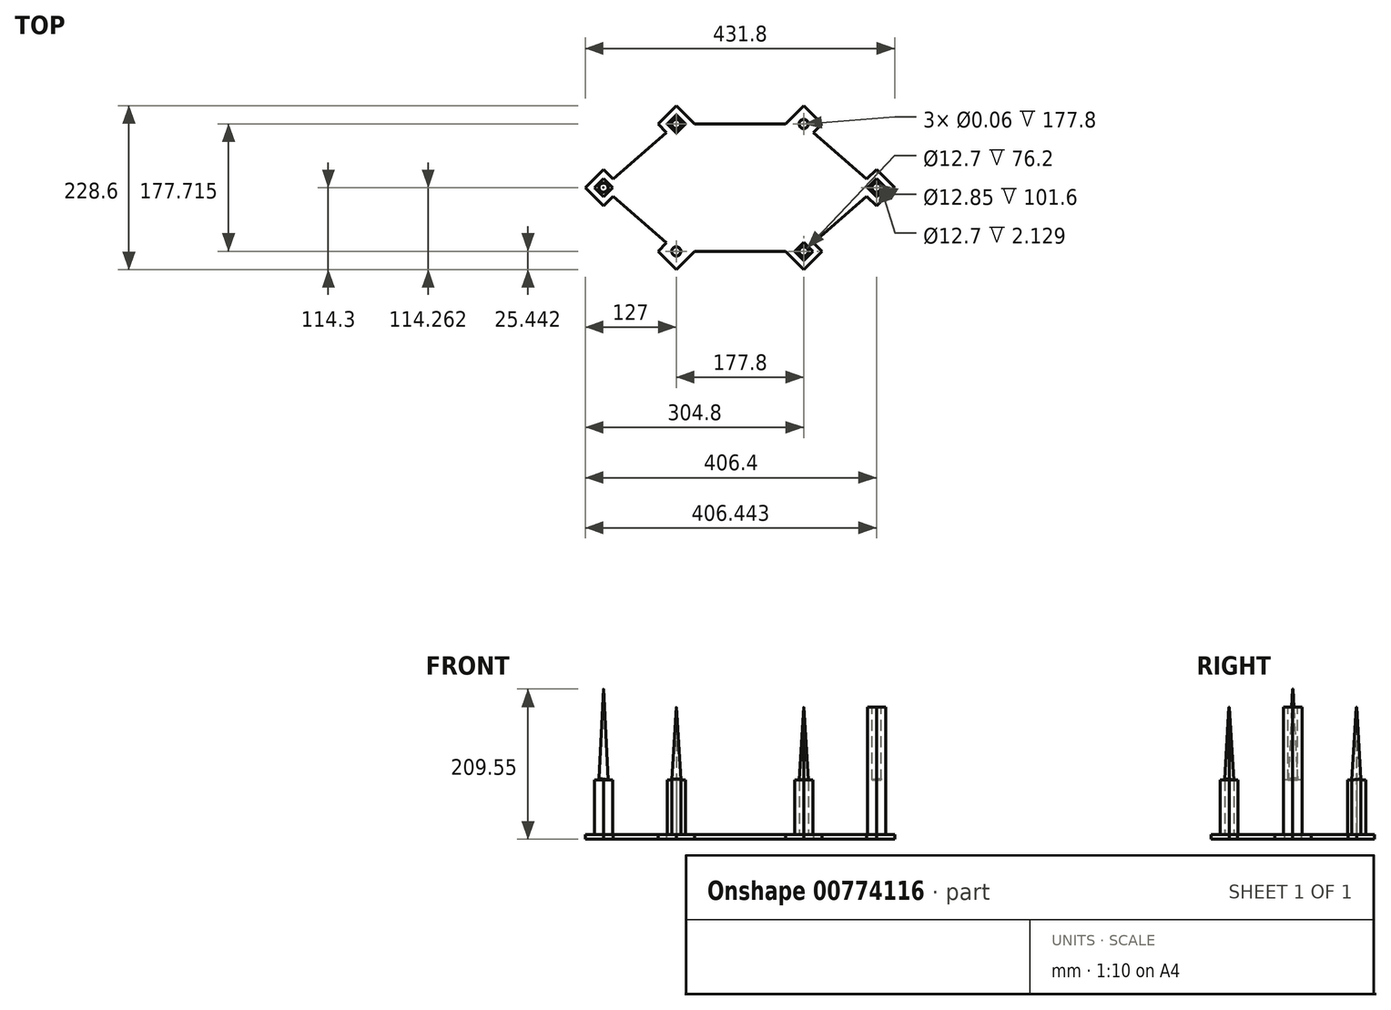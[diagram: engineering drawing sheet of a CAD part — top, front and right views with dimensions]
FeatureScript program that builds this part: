
annotation { "Feature Type Name" : "Feature", "Feature Type Description" : "" }
export const myFeature = defineFeature(function(context is Context, id is Id, definition is map)
    precondition{}
    {
        {
            var Q0;
            Q0=qCreatedBy(makeId("Top.planeOp"),FACE);
            var sketch = newSketch(context, id + "F0", { "sketchPlane" : qUnion([Q0])});
            skLineSegment(sketch, "E0", {"start": v(0, 88.9) * mm, "end": v(-63.5, 88.9) * mm});
            skLineSegment(sketch, "E1", {"start": v(-63.5, 88.9) * mm, "end": v(-88.9, 114.3) * mm});
            skLineSegment(sketch, "E2", {"start": v(-88.9, 114.3) * mm, "end": v(-114.3, 88.9) * mm});
            skLineSegment(sketch, "E3", {"start": v(-114.3, 88.9) * mm, "end": v(-88.9, 63.5) * mm});
            skLineSegment(sketch, "E4", {"start": v(-88.9, 63.5) * mm, "end": v(-63.5, 88.9) * mm});
            skLineSegment(sketch, "E5", {"start": v(-88.9, 63.5) * mm, "end": v(-88.9, 0) * mm});
            skLineSegment(sketch, "E6", {"start": v(-88.9, 88.9) * mm, "end": v(-190.5, 0) * mm});
            skLineSegment(sketch, "E7", {"start": v(-88.9, 114.3) * mm, "end": v(-88.9, 63.5) * mm, "construction": true});
            skLineSegment(sketch, "E8", {"start": v(-63.5, 88.9) * mm, "end": v(-114.3, 88.9) * mm, "construction": true});
            skLineSegment(sketch, "E9", {"start": v(-190.5, 25.4) * mm, "end": v(-215.9, 0) * mm});
            skLineSegment(sketch, "E10", {"start": v(-190.5, 25.4) * mm, "end": v(-165.1, 0) * mm});
            skLineSegment(sketch, "E11", {"start": v(-190.5, 25.4) * mm, "end": v(-190.5, 0) * mm, "construction": true});
            skPoint(sketch, "E12", {"position": v(-190.5, 0) * mm});
            skLineSegment(sketch, "E13.MirrorCS", {"start": v(-114.3, -88.9) * mm, "end": v(-88.9, -63.5) * mm});
            skLineSegment(sketch, "E14.MirrorCS", {"start": v(-88.9, -63.5) * mm, "end": v(-63.5, -88.9) * mm});
            skLineSegment(sketch, "E15.MirrorCS", {"start": v(-63.5, -88.9) * mm, "end": v(-114.3, -88.9) * mm, "construction": true});
            skLineSegment(sketch, "E16.MirrorCS", {"start": v(-190.5, -25.4) * mm, "end": v(-165.1, 0) * mm});
            skLineSegment(sketch, "E17.MirrorCS", {"start": v(-63.5, -88.9) * mm, "end": v(-88.9, -114.3) * mm});
            skLineSegment(sketch, "E18.MirrorCS", {"start": v(-88.9, -114.3) * mm, "end": v(-88.9, -63.5) * mm, "construction": true});
            skLineSegment(sketch, "E19.MirrorCS", {"start": v(0, -88.9) * mm, "end": v(-63.5, -88.9) * mm});
            skLineSegment(sketch, "E20.MirrorCS", {"start": v(-88.9, -114.3) * mm, "end": v(-114.3, -88.9) * mm});
            skLineSegment(sketch, "E21.MirrorCS", {"start": v(-190.5, -25.4) * mm, "end": v(-215.9, 0) * mm});
            skLineSegment(sketch, "E22.MirrorCS", {"start": v(-88.9, -88.9) * mm, "end": v(-190.5, 0) * mm});
            skLineSegment(sketch, "E23.MirrorCS", {"start": v(-190.5, -25.4) * mm, "end": v(-190.5, 0) * mm, "construction": true});
            skLineSegment(sketch, "E24.MirrorCS", {"start": v(-88.9, -63.5) * mm, "end": v(-88.9, 0) * mm});
            skPoint(sketch, "E25.MirrorP", {"position": v(190.5, 0) * mm});
            skLineSegment(sketch, "E26.MirrorCS", {"start": v(63.5, 88.9) * mm, "end": v(114.3, 88.9) * mm, "construction": true});
            skLineSegment(sketch, "E27.MirrorCS", {"start": v(190.5, 25.4) * mm, "end": v(215.9, 0) * mm});
            skLineSegment(sketch, "E28.MirrorCS", {"start": v(63.5, -88.9) * mm, "end": v(114.3, -88.9) * mm, "construction": true});
            skLineSegment(sketch, "E29.MirrorCS", {"start": v(88.9, -63.5) * mm, "end": v(63.5, -88.9) * mm});
            skLineSegment(sketch, "E30.MirrorCS", {"start": v(190.5, 25.4) * mm, "end": v(165.1, 0) * mm});
            skLineSegment(sketch, "E31.MirrorCS", {"start": v(190.5, 25.4) * mm, "end": v(190.5, 0) * mm, "construction": true});
            skLineSegment(sketch, "E32.MirrorCS", {"start": v(114.3, -88.9) * mm, "end": v(88.9, -63.5) * mm});
            skLineSegment(sketch, "E33.MirrorCS", {"start": v(88.9, -63.5) * mm, "end": v(88.9, 0) * mm});
            skLineSegment(sketch, "E34.MirrorCS", {"start": v(190.5, -25.4) * mm, "end": v(190.5, 0) * mm, "construction": true});
            skLineSegment(sketch, "E35.MirrorCS", {"start": v(190.5, -25.4) * mm, "end": v(215.9, 0) * mm});
            skLineSegment(sketch, "E36.MirrorCS", {"start": v(190.5, -25.4) * mm, "end": v(165.1, 0) * mm});
            skLineSegment(sketch, "E37.MirrorCS", {"start": v(0, 88.9) * mm, "end": v(63.5, 88.9) * mm});
            skLineSegment(sketch, "E38.MirrorCS", {"start": v(114.3, 88.9) * mm, "end": v(88.9, 63.5) * mm});
            skLineSegment(sketch, "E39.MirrorCS", {"start": v(88.9, 63.5) * mm, "end": v(63.5, 88.9) * mm});
            skLineSegment(sketch, "E40.MirrorCS", {"start": v(88.9, -88.9) * mm, "end": v(190.5, 0) * mm});
            skLineSegment(sketch, "E41.MirrorCS", {"start": v(88.9, 114.3) * mm, "end": v(88.9, 63.5) * mm, "construction": true});
            skLineSegment(sketch, "E42.MirrorCS", {"start": v(0, -88.9) * mm, "end": v(63.5, -88.9) * mm});
            skLineSegment(sketch, "E43.MirrorCS", {"start": v(63.5, 88.9) * mm, "end": v(88.9, 114.3) * mm});
            skLineSegment(sketch, "E44.MirrorCS", {"start": v(88.9, 114.3) * mm, "end": v(114.3, 88.9) * mm});
            skLineSegment(sketch, "E45.MirrorCS", {"start": v(63.5, -88.9) * mm, "end": v(88.9, -114.3) * mm});
            skLineSegment(sketch, "E46.MirrorCS", {"start": v(88.9, 88.9) * mm, "end": v(190.5, 0) * mm});
            skLineSegment(sketch, "E47.MirrorCS", {"start": v(88.9, -114.3) * mm, "end": v(114.3, -88.9) * mm});
            skLineSegment(sketch, "E48.MirrorCS", {"start": v(88.9, 63.5) * mm, "end": v(88.9, 0) * mm});
            skLineSegment(sketch, "E49.MirrorCS", {"start": v(88.9, -114.3) * mm, "end": v(88.9, -63.5) * mm, "construction": true});
            skSolve(sketch);
        }
        {
            var Q0;
            {var subQ5=sQuery(id+"F0.wireOp",EDGE,"E9");Q0=makeQuery(id+"F0.imprint","IMPRINT",FACE,{"disambiguationData":[TD([[makeQuery(id+"F0.imprint","IMPRINT",EDGE,{"derivedFrom":subQ5}),1.0]])]});}
            var Q1;
            {var subQ0=sQuery(id+"F0.wireOp",EDGE,"E22.MirrorCS");var subQ1=sQuery(id+"F0.wireOp",EDGE,"E6");var subQ2=makeQuery(id+"F0.imprint","INTERSECT",VERTEX,{"derivedFrom":[subQ1,subQ0]});Q1=makeQuery(id+"F0.imprint","IMPRINT",FACE,{"disambiguationData":[TD([[makeQuery(id+"F0.imprint","IMPRINT",EDGE,{"disambiguationData":[TD([[subQ2,1.0]])],"derivedFrom":subQ1}),1.0]])]});}
            var Q2;
            {var subQ7=sQuery(id+"F0.wireOp",EDGE,"E5");Q2=makeQuery(id+"F0.imprint","IMPRINT",FACE,{"disambiguationData":[TD([[makeQuery(id+"F0.imprint","IMPRINT",EDGE,{"derivedFrom":subQ7}),-1.0]])]});}
            var Q3;
            Q3=makeQuery(id+"F0.imprint","IMPRINT",FACE,{"disambiguationData":[TD([[makeQuery(id+"F0.imprint","IMPRINT",EDGE,{"derivedFrom":sQuery(id+"F0.wireOp",EDGE,"E1")}),1.0]])]});
            var Q4;
            {var subQ0=sQuery(id+"F0.wireOp",EDGE,"E14.MirrorCS");Q4=makeQuery(id+"F0.imprint","IMPRINT",FACE,{"disambiguationData":[TD([[makeQuery(id+"F0.imprint","IMPRINT",EDGE,{"derivedFrom":subQ0}),-1.0]])]});}
            var Q5;
            {var subQ1=sQuery(id+"F0.wireOp",EDGE,"E29.MirrorCS");Q5=makeQuery(id+"F0.imprint","IMPRINT",FACE,{"disambiguationData":[TD([[makeQuery(id+"F0.imprint","IMPRINT",EDGE,{"derivedFrom":subQ1}),1.0]])]});}
            var Q6;
            {var subQ9=sQuery(id+"F0.wireOp",EDGE,"E33.MirrorCS");Q6=makeQuery(id+"F0.imprint","IMPRINT",FACE,{"disambiguationData":[TD([[makeQuery(id+"F0.imprint","IMPRINT",EDGE,{"derivedFrom":subQ9}),-1.0]])]});}
            var Q7;
            Q7=makeQuery(id+"F0.imprint","IMPRINT",FACE,{"disambiguationData":[TD([[makeQuery(id+"F0.imprint","IMPRINT",EDGE,{"derivedFrom":sQuery(id+"F0.wireOp",EDGE,"E0")}),1.0]])]});
            var Q8;
            {var subQ0=sQuery(id+"F0.wireOp",EDGE,"E39.MirrorCS");Q8=makeQuery(id+"F0.imprint","IMPRINT",FACE,{"disambiguationData":[TD([[makeQuery(id+"F0.imprint","IMPRINT",EDGE,{"derivedFrom":subQ0}),-1.0]])]});}
            var Q9;
            {var subQ5=sQuery(id+"F0.wireOp",EDGE,"E27.MirrorCS");Q9=makeQuery(id+"F0.imprint","IMPRINT",FACE,{"disambiguationData":[TD([[makeQuery(id+"F0.imprint","IMPRINT",EDGE,{"derivedFrom":subQ5}),-1.0]])]});}
            var Q10;
            {var subQ0=sQuery(id+"F0.wireOp",EDGE,"E36.MirrorCS");var subQ1=sQuery(id+"F0.wireOp",EDGE,"E30.MirrorCS");var subQ2=makeQuery(id+"F0.imprint","INTERSECT",VERTEX,{"derivedFrom":[subQ1,subQ0]});Q10=makeQuery(id+"F0.imprint","IMPRINT",FACE,{"disambiguationData":[TD([[makeQuery(id+"F0.imprint","IMPRINT",EDGE,{"disambiguationData":[TD([[subQ2,1.0]])],"derivedFrom":subQ1}),1.0]])]});}
            extrude(context, id + "F1", {"entities" : qUnion([Q0, Q1, Q2, Q3, Q4, Q5, Q6, Q7, Q8, Q9, Q10]), "depth" : 228.6 * mm, "offsetDistance" : 25.4 * mm});
        }
        {
            var Q0;
            Q0=makeQuery(id+"F1.opExtrude","CAP_FACE",FACE,{"disambiguationData":[OSD([sQuery(id+"F0.wireOp",EDGE,"E0"),sQuery(id+"F0.wireOp",EDGE,"E1"),sQuery(id+"F0.wireOp",EDGE,"E2"),sQuery(id+"F0.wireOp",EDGE,"E3"),sQuery(id+"F0.wireOp",EDGE,"E6"),sQuery(id+"F0.wireOp",EDGE,"E9"),sQuery(id+"F0.wireOp",EDGE,"E10"),sQuery(id+"F0.wireOp",EDGE,"E13.MirrorCS"),sQuery(id+"F0.wireOp",EDGE,"E16.MirrorCS"),sQuery(id+"F0.wireOp",EDGE,"E17.MirrorCS"),sQuery(id+"F0.wireOp",EDGE,"E19.MirrorCS"),sQuery(id+"F0.wireOp",EDGE,"E20.MirrorCS"),sQuery(id+"F0.wireOp",EDGE,"E21.MirrorCS"),sQuery(id+"F0.wireOp",EDGE,"E22.MirrorCS"),sQuery(id+"F0.wireOp",EDGE,"E27.MirrorCS"),sQuery(id+"F0.wireOp",EDGE,"E30.MirrorCS"),sQuery(id+"F0.wireOp",EDGE,"E32.MirrorCS"),sQuery(id+"F0.wireOp",EDGE,"E35.MirrorCS"),sQuery(id+"F0.wireOp",EDGE,"E36.MirrorCS"),sQuery(id+"F0.wireOp",EDGE,"E37.MirrorCS"),sQuery(id+"F0.wireOp",EDGE,"E38.MirrorCS"),sQuery(id+"F0.wireOp",EDGE,"E40.MirrorCS"),sQuery(id+"F0.wireOp",EDGE,"E42.MirrorCS"),sQuery(id+"F0.wireOp",EDGE,"E43.MirrorCS"),sQuery(id+"F0.wireOp",EDGE,"E44.MirrorCS"),sQuery(id+"F0.wireOp",EDGE,"E45.MirrorCS"),sQuery(id+"F0.wireOp",EDGE,"E46.MirrorCS"),sQuery(id+"F0.wireOp",EDGE,"E47.MirrorCS")])],"isStart":false});
            var sketch = newSketch(context, id + "F2", { "sketchPlane" : qUnion([Q0])});
            skLineSegment(sketch, "E50", {"start": v(-101.6, 88.9) * mm, "end": v(-88.9, 76.2) * mm});
            skLineSegment(sketch, "E51", {"start": v(-88.9, 76.2) * mm, "end": v(-76.2, 88.9) * mm});
            skLineSegment(sketch, "E52", {"start": v(-76.2, 88.9) * mm, "end": v(-88.9, 101.6) * mm});
            skLineSegment(sketch, "E53", {"start": v(-88.9, 101.6) * mm, "end": v(-101.6, 88.9) * mm});
            skCircle(sketch, "E54", {"center": v(-88.9, 88.86) * mm, "radius": 6.35 * mm});
            skCircle(sketch, "E55", {"center": v(-88.9, 88.86) * mm, "radius": 0.03 * mm});
            skCircle(sketch, "E56.MirrorC", {"center": v(-88.9, -88.86) * mm, "radius": 0.03 * mm});
            skCircle(sketch, "E57.MirrorC", {"center": v(-88.9, -88.86) * mm, "radius": 6.35 * mm});
            skLineSegment(sketch, "E58.MirrorCS", {"start": v(-88.9, -101.6) * mm, "end": v(-101.6, -88.9) * mm});
            skLineSegment(sketch, "E59.MirrorCS", {"start": v(-76.2, -88.9) * mm, "end": v(-88.9, -101.6) * mm});
            skLineSegment(sketch, "E60.MirrorCS", {"start": v(-88.9, -76.2) * mm, "end": v(-76.2, -88.9) * mm});
            skLineSegment(sketch, "E61.MirrorCS", {"start": v(-101.6, -88.9) * mm, "end": v(-88.9, -76.2) * mm});
            skCircle(sketch, "E62.MirrorC", {"center": v(88.9, 88.86) * mm, "radius": 0.03 * mm});
            skCircle(sketch, "E63.MirrorC", {"center": v(88.9, -88.86) * mm, "radius": 0.03 * mm});
            skCircle(sketch, "E64.MirrorC", {"center": v(88.9, 88.86) * mm, "radius": 6.35 * mm});
            skLineSegment(sketch, "E65.MirrorCS", {"start": v(88.9, 101.6) * mm, "end": v(101.6, 88.9) * mm});
            skLineSegment(sketch, "E66.MirrorCS", {"start": v(76.2, 88.9) * mm, "end": v(88.9, 101.6) * mm});
            skLineSegment(sketch, "E67.MirrorCS", {"start": v(88.9, 76.2) * mm, "end": v(76.2, 88.9) * mm});
            skLineSegment(sketch, "E68.MirrorCS", {"start": v(101.6, 88.9) * mm, "end": v(88.9, 76.2) * mm});
            skLineSegment(sketch, "E69.MirrorCS", {"start": v(101.6, -88.9) * mm, "end": v(88.9, -76.2) * mm});
            skLineSegment(sketch, "E70.MirrorCS", {"start": v(76.2, -88.9) * mm, "end": v(88.9, -101.6) * mm});
            skLineSegment(sketch, "E71.MirrorCS", {"start": v(88.9, -76.2) * mm, "end": v(76.2, -88.9) * mm});
            skCircle(sketch, "E72.MirrorC", {"center": v(88.9, -88.86) * mm, "radius": 6.35 * mm});
            skLineSegment(sketch, "E73.MirrorCS", {"start": v(88.9, -101.6) * mm, "end": v(101.6, -88.9) * mm});
            skLineSegment(sketch, "E74", {"start": v(-190.5, 12.7) * mm, "end": v(-203.2, 0) * mm});
            skLineSegment(sketch, "E75", {"start": v(-203.2, 0) * mm, "end": v(-190.5, -12.7) * mm});
            skLineSegment(sketch, "E76", {"start": v(-190.5, -12.7) * mm, "end": v(-177.8, 0) * mm});
            skLineSegment(sketch, "E77", {"start": v(-190.5, 12.7) * mm, "end": v(-177.8, 0) * mm});
            skCircle(sketch, "E78", {"center": v(-190.5, 0) * mm, "radius": 6.35 * mm});
            skCircle(sketch, "E79.MirrorC", {"center": v(190.5, 0) * mm, "radius": 6.35 * mm});
            skLineSegment(sketch, "E80.MirrorCS", {"start": v(203.2, 0) * mm, "end": v(190.5, -12.7) * mm});
            skLineSegment(sketch, "E81.MirrorCS", {"start": v(190.5, 12.7) * mm, "end": v(177.8, 0) * mm});
            skLineSegment(sketch, "E82.MirrorCS", {"start": v(190.5, -12.7) * mm, "end": v(177.8, 0) * mm});
            skLineSegment(sketch, "E83.MirrorCS", {"start": v(190.5, 12.7) * mm, "end": v(203.2, 0) * mm});
            skSolve(sketch);
        }
        {
            var Q0;
            Q0=makeQuery(id+"F2.imprint","IMPRINT",FACE,{"disambiguationData":[TD([[makeQuery(id+"F2.imprint","IMPRINT",EDGE,{"derivedFrom":sQuery(id+"F2.wireOp",EDGE,"E74")}),1.0]])]});
            var Q1;
            Q1=makeQuery(id+"F2.imprint","IMPRINT",FACE,{"disambiguationData":[TD([[makeQuery(id+"F2.imprint","IMPRINT",EDGE,{"derivedFrom":sQuery(id+"F2.wireOp",EDGE,"E50")}),1.0]])]});
            var Q2;
            Q2=makeQuery(id+"F2.imprint","IMPRINT",FACE,{"disambiguationData":[TD([[makeQuery(id+"F2.imprint","IMPRINT",EDGE,{"derivedFrom":sQuery(id+"F2.wireOp",EDGE,"E79.MirrorC")}),1.0]])]});
            var Q3;
            Q3=makeQuery(id+"F2.imprint","IMPRINT",FACE,{"disambiguationData":[TD([[makeQuery(id+"F2.imprint","IMPRINT",EDGE,{"derivedFrom":sQuery(id+"F2.wireOp",EDGE,"E69.MirrorCS")}),1.0]])]});
            var Q4;
            Q4=makeQuery(id+"F2.imprint","IMPRINT",FACE,{"disambiguationData":[TD([[makeQuery(id+"F2.imprint","IMPRINT",EDGE,{"derivedFrom":sQuery(id+"F2.wireOp",EDGE,"E57.MirrorC")}),1.0]])]});
            var Q5;
            Q5=makeQuery(id+"F2.imprint","IMPRINT",FACE,{"disambiguationData":[TD([[makeQuery(id+"F2.imprint","IMPRINT",EDGE,{"derivedFrom":sQuery(id+"F2.wireOp",EDGE,"E64.MirrorC")}),1.0]])]});
            extrude(context, id + "F3", {"entities" : qUnion([Q0, Q1, Q2, Q3, Q4, Q5]), "operationType" : NewBodyOperationType.ADD, "depth" : 76.2 * mm, "offsetDistance" : 25.4 * mm});
        }
        {
            var Q0;
            Q0=makeQuery(id+"F2.imprint","IMPRINT",FACE,{"disambiguationData":[TD([[makeQuery(id+"F2.imprint","IMPRINT",EDGE,{"derivedFrom":sQuery(id+"F2.wireOp",EDGE,"E54")}),1.0]])]});
            var Q1;
            Q1=makeQuery(id+"F2.imprint","IMPRINT",FACE,{"disambiguationData":[TD([[makeQuery(id+"F2.imprint","IMPRINT",EDGE,{"derivedFrom":sQuery(id+"F2.wireOp",EDGE,"E79.MirrorC")}),-1.0]])]});
            var Q2;
            Q2=makeQuery(id+"F2.imprint","IMPRINT",FACE,{"disambiguationData":[TD([[makeQuery(id+"F2.imprint","IMPRINT",EDGE,{"derivedFrom":sQuery(id+"F2.wireOp",EDGE,"E56.MirrorC")}),-1.0]])]});
            var Q3;
            Q3=makeQuery(id+"F2.imprint","IMPRINT",FACE,{"disambiguationData":[TD([[makeQuery(id+"F2.imprint","IMPRINT",EDGE,{"derivedFrom":sQuery(id+"F2.wireOp",EDGE,"E63.MirrorC")}),1.0]])]});
            var Q4;
            Q4=makeQuery(id+"F2.imprint","IMPRINT",FACE,{"disambiguationData":[TD([[makeQuery(id+"F2.imprint","IMPRINT",EDGE,{"derivedFrom":sQuery(id+"F2.wireOp",EDGE,"E62.MirrorC")}),-1.0]])]});
            extrude(context, id + "F4", {"entities" : qUnion([Q0, Q1, Q2, Q3, Q4]), "operationType" : NewBodyOperationType.ADD, "depth" : 177.8 * mm, "offsetDistance" : 25.4 * mm});
        }
        {
            var Q0;
            Q0=makeQuery(id+"F2.imprint","IMPRINT",FACE,{"disambiguationData":[TD([[makeQuery(id+"F2.imprint","IMPRINT",EDGE,{"derivedFrom":sQuery(id+"F2.wireOp",EDGE,"E78")}),1.0]])]});
            extrude(context, id + "F5", {"entities" : qUnion([Q0]), "operationType" : NewBodyOperationType.ADD, "depth" : 203.2 * mm, "offsetDistance" : 25.4 * mm});
        }
        {
            var Q0;
            Q0=makeQuery(id+"F1.opExtrude","SWEPT_FACE",FACE,{"disambiguationData":[OSD([sQuery(id+"F0.wireOp",EDGE,"E19.MirrorCS"),sQuery(id+"F0.wireOp",EDGE,"E42.MirrorCS")])]});
            var sketch = newSketch(context, id + "F6", { "sketchPlane" : qUnion([Q0])});
            skLineSegment(sketch, "E84.bottom", {"start": v(-88.9, 304.8) * mm, "end": v(-82.5, 304.8) * mm});
            skLineSegment(sketch, "E84.top", {"start": v(-88.9, 406.4) * mm, "end": v(-82.5, 406.4) * mm});
            skLineSegment(sketch, "E84.left", {"start": v(-88.9, 304.8) * mm, "end": v(-88.9, 406.4) * mm});
            skLineSegment(sketch, "E84.right", {"start": v(-82.5, 304.8) * mm, "end": v(-82.5, 406.4) * mm});
            skLineSegment(sketch, "E85", {"start": v(-88.87, 406.4) * mm, "end": v(-82.5, 304.8) * mm});
            skSolve(sketch);
        }
        {
            var Q0;
            {var subQ0=sQuery(id+"F6.wireOp",EDGE,"E84.right");Q0=makeQuery(id+"F6.imprint","IMPRINT",FACE,{"disambiguationData":[TD([[makeQuery(id+"F6.imprint","IMPRINT",EDGE,{"derivedFrom":subQ0}),1.0]])]});}
            var Q1;
            Q1=sQuery(id+"F6.wireOp",EDGE,"E84.left");
            revolve(context, id + "F7", {"operationType" : NewBodyOperationType.REMOVE, "surfaceOperationType" : NewSurfaceOperationType.NEW, "entities" : qUnion([Q0]), "axis" : qUnion([Q1]), "revolveType" : RevolveType.FULL, "oppositeDirection" : true});
        }
        {
            var Q0;
            Q0=makeQuery(id+"F1.opExtrude","SWEPT_FACE",FACE,{"disambiguationData":[OSD([sQuery(id+"F0.wireOp",EDGE,"E19.MirrorCS"),sQuery(id+"F0.wireOp",EDGE,"E42.MirrorCS")])]});
            var sketch = newSketch(context, id + "F8", { "sketchPlane" : qUnion([Q0])});
            skLineSegment(sketch, "E86.bottom", {"start": v(88.9, 304.8) * mm, "end": v(95.3, 304.8) * mm});
            skLineSegment(sketch, "E86.top", {"start": v(88.9, 406.4) * mm, "end": v(95.3, 406.4) * mm});
            skLineSegment(sketch, "E86.left", {"start": v(88.9, 304.8) * mm, "end": v(88.9, 406.4) * mm});
            skLineSegment(sketch, "E86.right", {"start": v(95.3, 304.8) * mm, "end": v(95.3, 406.4) * mm});
            skLineSegment(sketch, "E87", {"start": v(88.93, 406.4) * mm, "end": v(95.3, 304.8) * mm});
            skSolve(sketch);
        }
        {
            var Q0;
            {var subQ0=sQuery(id+"F8.wireOp",EDGE,"E86.right");Q0=makeQuery(id+"F8.imprint","IMPRINT",FACE,{"disambiguationData":[TD([[makeQuery(id+"F8.imprint","IMPRINT",EDGE,{"derivedFrom":subQ0}),1.0]])]});}
            var Q1;
            Q1=sQuery(id+"F8.wireOp",EDGE,"E86.left");
            revolve(context, id + "F9", {"operationType" : NewBodyOperationType.REMOVE, "surfaceOperationType" : NewSurfaceOperationType.NEW, "entities" : qUnion([Q0]), "axis" : qUnion([Q1]), "revolveType" : RevolveType.FULL, "oppositeDirection" : true});
        }
        {
            var Q0;
            Q0=makeQuery(id+"F1.opExtrude","SWEPT_FACE",FACE,{"disambiguationData":[OSD([sQuery(id+"F0.wireOp",EDGE,"E0"),sQuery(id+"F0.wireOp",EDGE,"E37.MirrorCS")])]});
            var sketch = newSketch(context, id + "F10", { "sketchPlane" : qUnion([Q0])});
            skLineSegment(sketch, "E88.bottom", {"start": v(88.9, 304.8) * mm, "end": v(95.3, 304.8) * mm});
            skLineSegment(sketch, "E88.top", {"start": v(88.9, 406.4) * mm, "end": v(95.3, 406.4) * mm});
            skLineSegment(sketch, "E88.left", {"start": v(88.9, 304.8) * mm, "end": v(88.9, 406.4) * mm});
            skLineSegment(sketch, "E88.right", {"start": v(95.3, 304.8) * mm, "end": v(95.3, 406.4) * mm});
            skLineSegment(sketch, "E89", {"start": v(88.93, 406.4) * mm, "end": v(95.3, 304.8) * mm});
            skSolve(sketch);
        }
        {
            var Q0;
            {var subQ0=sQuery(id+"F10.wireOp",EDGE,"E88.right");Q0=makeQuery(id+"F10.imprint","IMPRINT",FACE,{"disambiguationData":[TD([[makeQuery(id+"F10.imprint","IMPRINT",EDGE,{"derivedFrom":subQ0}),1.0]])]});}
            var Q1;
            Q1=sQuery(id+"F10.wireOp",EDGE,"E88.left");
            revolve(context, id + "F11", {"operationType" : NewBodyOperationType.REMOVE, "surfaceOperationType" : NewSurfaceOperationType.NEW, "entities" : qUnion([Q0]), "axis" : qUnion([Q1]), "revolveType" : RevolveType.FULL, "oppositeDirection" : true});
        }
        {
            var Q0;
            Q0=makeQuery(id+"F1.opExtrude","SWEPT_FACE",FACE,{"disambiguationData":[OSD([sQuery(id+"F0.wireOp",EDGE,"E0"),sQuery(id+"F0.wireOp",EDGE,"E37.MirrorCS")])]});
            var sketch = newSketch(context, id + "F12", { "sketchPlane" : qUnion([Q0])});
            skLineSegment(sketch, "E90.bottom", {"start": v(-82.5, 304.8) * mm, "end": v(-88.9, 304.8) * mm});
            skLineSegment(sketch, "E90.top", {"start": v(-82.5, 406.4) * mm, "end": v(-88.9, 406.4) * mm});
            skLineSegment(sketch, "E90.left", {"start": v(-82.5, 304.8) * mm, "end": v(-82.5, 406.4) * mm});
            skLineSegment(sketch, "E90.right", {"start": v(-88.9, 304.8) * mm, "end": v(-88.9, 406.4) * mm});
            skLineSegment(sketch, "E91", {"start": v(-88.87, 406.4) * mm, "end": v(-82.5, 304.8) * mm});
            skSolve(sketch);
        }
        {
            var Q0;
            {var subQ0=sQuery(id+"F12.wireOp",EDGE,"E90.left");Q0=makeQuery(id+"F12.imprint","IMPRINT",FACE,{"disambiguationData":[TD([[makeQuery(id+"F12.imprint","IMPRINT",EDGE,{"derivedFrom":subQ0}),1.0]])]});}
            var Q1;
            Q1=sQuery(id+"F12.wireOp",EDGE,"E90.right");
            revolve(context, id + "F13", {"operationType" : NewBodyOperationType.REMOVE, "surfaceOperationType" : NewSurfaceOperationType.NEW, "entities" : qUnion([Q0]), "axis" : qUnion([Q1]), "revolveType" : RevolveType.FULL, "oppositeDirection" : true});
        }
        {
            var Q0;
            Q0=makeQuery(id+"F1.opExtrude","SWEPT_FACE",FACE,{"disambiguationData":[OSD([sQuery(id+"F0.wireOp",EDGE,"E46.MirrorCS")])]});
            var sketch = newSketch(context, id + "F14", { "sketchPlane" : qUnion([Q0])});
            skLineSegment(sketch, "E92.bottom", {"start": v(-143.42, 304.8) * mm, "end": v(-137, 304.8) * mm});
            skLineSegment(sketch, "E92.top", {"start": v(-143.42, 406.4) * mm, "end": v(-137, 406.4) * mm});
            skLineSegment(sketch, "E92.left", {"start": v(-143.42, 304.8) * mm, "end": v(-143.42, 406.4) * mm});
            skLineSegment(sketch, "E92.right", {"start": v(-137, 304.8) * mm, "end": v(-137, 406.4) * mm});
            skLineSegment(sketch, "E93", {"start": v(-143.4, 406.4) * mm, "end": v(-137, 304.8) * mm});
            skSolve(sketch);
        }
        {
            var Q0;
            {var subQ0=sQuery(id+"F14.wireOp",EDGE,"E92.right");Q0=makeQuery(id+"F14.imprint","IMPRINT",FACE,{"disambiguationData":[TD([[makeQuery(id+"F14.imprint","IMPRINT",EDGE,{"derivedFrom":subQ0}),1.0]])]});}
            var Q1;
            Q1=sQuery(id+"F14.wireOp",EDGE,"E92.left");
            revolve(context, id + "F15", {"operationType" : NewBodyOperationType.REMOVE, "surfaceOperationType" : NewSurfaceOperationType.NEW, "entities" : qUnion([Q0]), "axis" : qUnion([Q1]), "revolveType" : RevolveType.FULL, "oppositeDirection" : true});
        }
        {
            var Q0;
            Q0=makeQuery(id+"F1.opExtrude","SWEPT_FACE",FACE,{"disambiguationData":[OSD([sQuery(id+"F0.wireOp",EDGE,"E22.MirrorCS")])]});
            var sketch = newSketch(context, id + "F16", { "sketchPlane" : qUnion([Q0])});
            skLineSegment(sketch, "E94.bottom", {"start": v(-143.42, 304.8) * mm, "end": v(-137, 304.8) * mm});
            skLineSegment(sketch, "E94.top", {"start": v(-143.42, 431.8) * mm, "end": v(-137, 431.8) * mm});
            skLineSegment(sketch, "E94.left", {"start": v(-143.42, 304.8) * mm, "end": v(-143.42, 431.8) * mm});
            skLineSegment(sketch, "E94.right", {"start": v(-137, 304.8) * mm, "end": v(-137, 431.8) * mm});
            skLineSegment(sketch, "E95", {"start": v(-143.4, 431.8) * mm, "end": v(-137, 304.8) * mm});
            skSolve(sketch);
        }
        {
            var Q0;
            {var subQ0=sQuery(id+"F16.wireOp",EDGE,"E94.right");Q0=makeQuery(id+"F16.imprint","IMPRINT",FACE,{"disambiguationData":[TD([[makeQuery(id+"F16.imprint","IMPRINT",EDGE,{"derivedFrom":subQ0}),1.0]])]});}
            var Q1;
            Q1=sQuery(id+"F16.wireOp",EDGE,"E94.left");
            revolve(context, id + "F17", {"operationType" : NewBodyOperationType.REMOVE, "surfaceOperationType" : NewSurfaceOperationType.NEW, "entities" : qUnion([Q0]), "axis" : qUnion([Q1]), "revolveType" : RevolveType.FULL, "oppositeDirection" : true});
        }
        {
            var Q0;
            Q0=qCreatedBy(makeId("Front.planeOp"),FACE);
            var sketch = newSketch(context, id + "F18", { "sketchPlane" : qUnion([Q0])});
            skLineSegment(sketch, "E96.bottom", {"start": v(-228.6, 222.25) * mm, "end": v(228.6, 222.25) * mm});
            skLineSegment(sketch, "E96.top", {"start": v(-228.6, -12.7) * mm, "end": v(228.6, -12.7) * mm});
            skLineSegment(sketch, "E96.left", {"start": v(-228.6, 222.25) * mm, "end": v(-228.6, -12.7) * mm});
            skLineSegment(sketch, "E96.right", {"start": v(228.6, 222.25) * mm, "end": v(228.6, -12.7) * mm});
            skSolve(sketch);
        }
        {
            var Q0;
            Q0 = qSketchRegion(id + "F18", true);
            extrude(context, id + "F19", {"entities" : qUnion([Q0]), "operationType" : NewBodyOperationType.REMOVE, "endBound" : BoundingType.SYMMETRIC, "oppositeDirection" : true, "depth" : 508 * mm, "offsetDistance" : 25.4 * mm});
        }
    });
